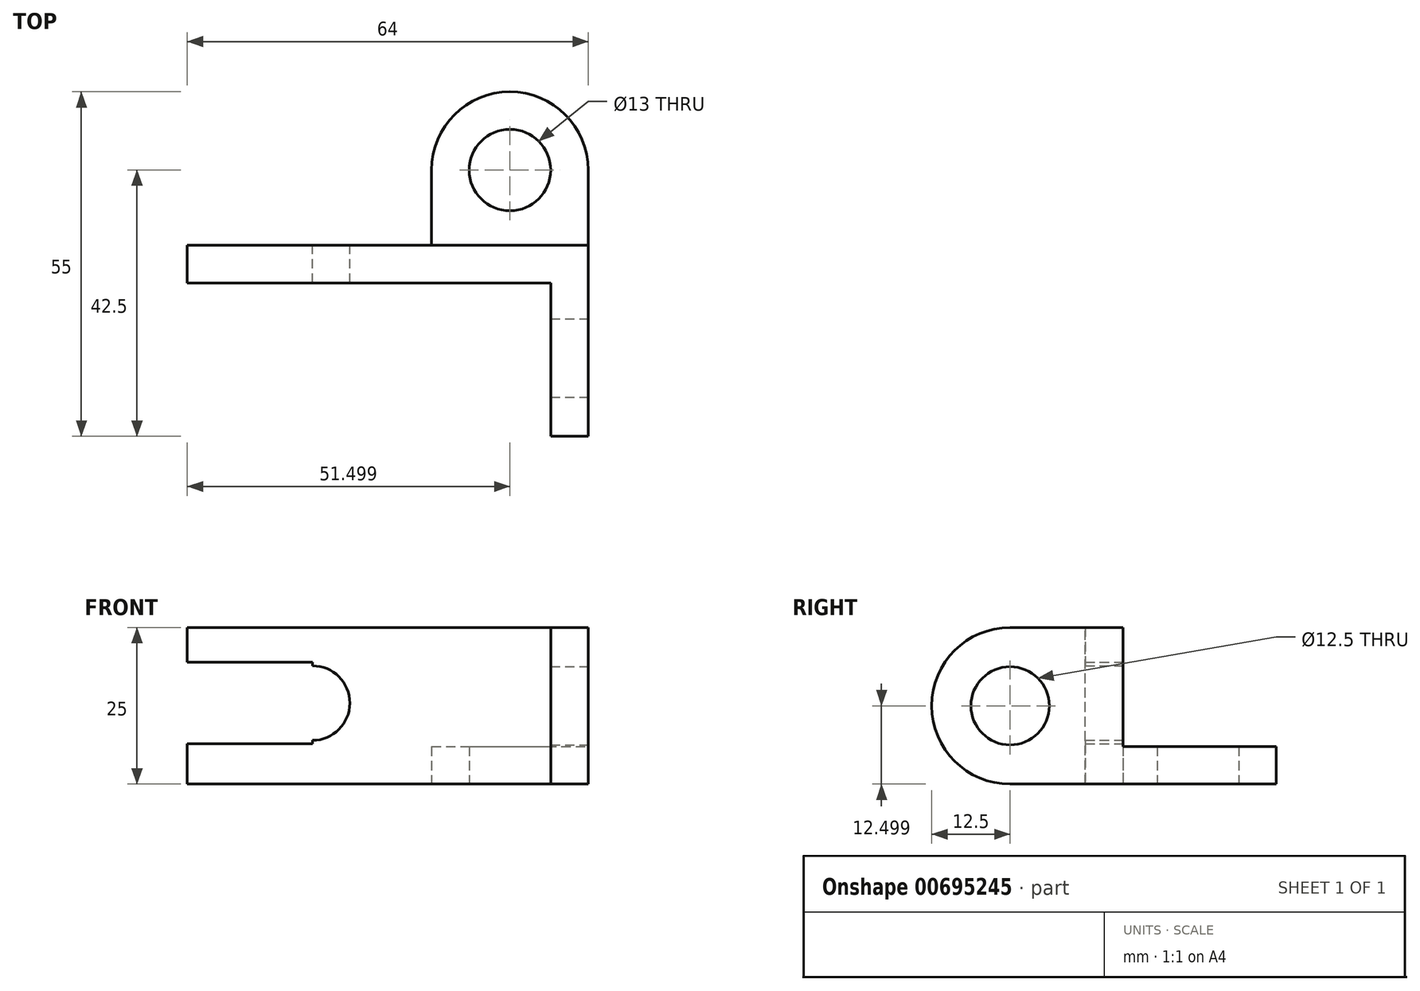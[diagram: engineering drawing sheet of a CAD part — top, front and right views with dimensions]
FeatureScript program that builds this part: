
annotation { "Feature Type Name" : "Feature", "Feature Type Description" : "" }
export const myFeature = defineFeature(function(context is Context, id is Id, definition is map)
    precondition{}
    {
        {
            var Q0;
            Q0=qCreatedBy(makeId("Front.planeOp"),FACE);
            var sketch = newSketch(context, id + "F0", { "sketchPlane" : qUnion([Q0])});
            skLineSegment(sketch, "E0.bottom", {"start": v(36.09, 12.07) * mm, "end": v(-27.91, 12.07) * mm});
            skLineSegment(sketch, "E0.top", {"start": v(36.09, -12.93) * mm, "end": v(-27.91, -12.93) * mm});
            skLineSegment(sketch, "E0.left", {"start": v(36.09, 12.07) * mm, "end": v(36.09, -12.93) * mm});
            skLineSegment(sketch, "E0.right", {"start": v(-27.91, 12.07) * mm, "end": v(-27.91, -12.93) * mm});
            skLineSegment(sketch, "E1.bottom", {"start": v(-27.91, 6.5) * mm, "end": v(-7.91, 6.5) * mm});
            skLineSegment(sketch, "E1.top", {"start": v(-27.91, -6.5) * mm, "end": v(-7.91, -6.5) * mm});
            skLineSegment(sketch, "E1.left", {"start": v(-27.91, 6.5) * mm, "end": v(-27.91, -6.5) * mm});
            skLineSegment(sketch, "E1.right", {"start": v(-7.91, 6.5) * mm, "end": v(-7.91, -6.5) * mm});
            skPoint(sketch, "E1.middle", {"position": v(-17.91, 0) * mm});
            skCircle(sketch, "E2", {"center": v(-7.91, 0) * mm, "radius": 5.95 * mm});
            skSolve(sketch);
        }
        {
            var Q0;
            {var subQ1=sQuery(id+"F0.wireOp",EDGE,"E0.bottom");Q0=makeQuery(id+"F0.imprint","IMPRINT",FACE,{"disambiguationData":[TD([[makeQuery(id+"F0.imprint","IMPRINT",EDGE,{"derivedFrom":subQ1}),1.0]])]});}
            extrude(context, id + "F1", {"entities" : qUnion([Q0]), "depth" : 6 * mm, "offsetDistance" : 25 * mm});
        }
        {
            var Q0;
            Q0=makeQuery(id+"F1.opExtrude","SWEPT_FACE",FACE,{"disambiguationData":[OSD([sQuery(id+"F0.wireOp",EDGE,"E0.left")])]});
            var sketch = newSketch(context, id + "F2", { "sketchPlane" : qUnion([Q0])});
            skLineSegment(sketch, "E3.bottom", {"start": v(0, 12.07) * mm, "end": v(-18, 12.07) * mm});
            skLineSegment(sketch, "E3.top", {"start": v(0, -12.93) * mm, "end": v(-18, -12.93) * mm});
            skLineSegment(sketch, "E3.left", {"start": v(0, 12.07) * mm, "end": v(0, -12.93) * mm});
            skLineSegment(sketch, "E3.right", {"start": v(-18, 12.07) * mm, "end": v(-18, -12.93) * mm});
            skCircle(sketch, "E4", {"center": v(-18, -0.43) * mm, "radius": 12.5 * mm});
            skCircle(sketch, "E5", {"center": v(-18, -0.43) * mm, "radius": 6.25 * mm});
            skSolve(sketch);
        }
        {
            var Q0;
            Q0 = qSketchRegion(id + "F2", true);
            extrude(context, id + "F3", {"entities" : qUnion([Q0]), "operationType" : NewBodyOperationType.ADD, "oppositeDirection" : true, "depth" : 6 * mm, "offsetDistance" : 25 * mm});
        }
        {
            var Q0;
            Q0=makeQuery(id+"F3.boolean.opBoolean","MERGE",FACE,{"derivedFrom":[makeQuery(id+"F1.opExtrude","SWEPT_FACE",FACE,{"disambiguationData":[OSD([sQuery(id+"F0.wireOp",EDGE,"E0.top")])]}),makeQuery(id+"F3.opExtrude","SWEPT_FACE",FACE,{"disambiguationData":[OSD([sQuery(id+"F2.wireOp",EDGE,"E3.top")])]})]});
            var sketch = newSketch(context, id + "F4", { "sketchPlane" : qUnion([Q0])});
            skLineSegment(sketch, "E6.bottom", {"start": v(36.09, 6) * mm, "end": v(11.09, 6) * mm});
            skLineSegment(sketch, "E6.top", {"start": v(36.09, -12) * mm, "end": v(11.09, -12) * mm});
            skLineSegment(sketch, "E6.left", {"start": v(36.09, 6) * mm, "end": v(36.09, -12) * mm});
            skLineSegment(sketch, "E6.right", {"start": v(11.09, 6) * mm, "end": v(11.09, -12) * mm});
            skArc(sketch, "E7", {"start": v(11.09, -12) * mm, "mid": v(23.59, -24.5) * mm, "end": v(36.09, -12) * mm});
            skSolve(sketch);
        }
        {
            var Q0;
            {var subQ0=sQuery(id+"F4.wireOp",EDGE,"E6.top");Q0=makeQuery(id+"F4.imprint","IMPRINT",FACE,{"disambiguationData":[TD([[makeQuery(id+"F4.imprint","IMPRINT",EDGE,{"derivedFrom":subQ0}),-1.0]])]});}
            var Q1;
            Q1 = qSketchRegion(id + "F4", true);
            extrude(context, id + "F5", {"entities" : qUnion([Q0, Q1]), "operationType" : NewBodyOperationType.ADD, "oppositeDirection" : true, "depth" : 6 * mm, "offsetDistance" : 25 * mm});
        }
        {
            var Q0;
            Q0=sQuery(id+"F4.wireOp",VERTEX,"E7.center");
            var Q1;
            Q1=makeQuery(id+"F1.opExtrude","SWEPT_BODY",BODY,{"disambiguationData":[OSD([sQuery(id+"F0.wireOp",EDGE,"E0.bottom"),sQuery(id+"F0.wireOp",EDGE,"E0.top"),sQuery(id+"F0.wireOp",EDGE,"E0.left"),sQuery(id+"F0.wireOp",EDGE,"E0.right"),sQuery(id+"F0.wireOp",EDGE,"E1.bottom"),sQuery(id+"F0.wireOp",EDGE,"E1.top"),sQuery(id+"F0.wireOp",EDGE,"E1.right"),sQuery(id+"F0.wireOp",EDGE,"E2")])]});
            hole(context, id + "F6", {"style" : HoleStyle.SIMPLE, "endStyle" : HoleEndStyle.THROUGH, "holeDiameter" : 13 * mm, "majorDiameter" : 5 * mm, "isTappedThrough" : true, "tappedDepth" : 12 * mm, "tapClearance" : 3, "locations" : qUnion([Q0]), "scope" : qUnion([Q1])});
        }
    });
